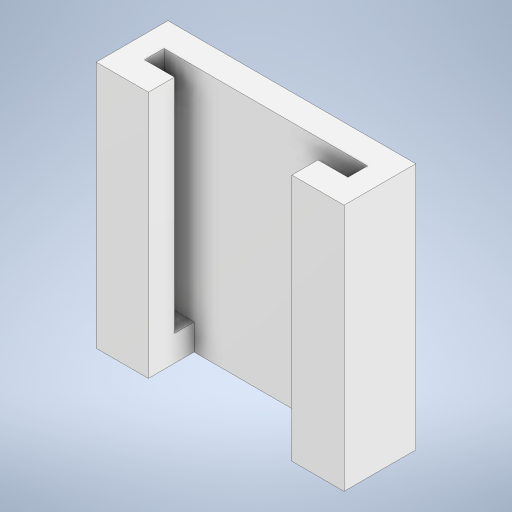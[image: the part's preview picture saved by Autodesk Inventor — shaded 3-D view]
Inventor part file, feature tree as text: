
AUTODESK INVENTOR PART (.ipt)
format: ipt  version: 2024 (Build 280153000, 153)  size: 504,320 bytes
history: native  units: mm
features: extrude x3, sketch x3, move_body x2, other x2, boolean_combine x1
ambient origin geometry x8: Origin, YZ Plane, XZ Plane, XY Plane, X Axis, Y Axis, Z Axis, Center Point
bodies: Solid1 (feature_tree), Solid2 (feature_tree)
feature tree (11):
  move_body  "Move Body1"
  move_body  "Move Body2"
  boolean_combine  "Combine1"
  extrude  "Extrusion1"  Depth=2.0mm TaperAngle=0.0deg
  extrude  "Extrusion2"  Depth=2.0mm TaperAngle=0.0deg
  extrude  "Extrusion5"  Depth=17.0mm
  sketch  "Sketch1"  dims[d0=9.5mm d1=-6.0mm d2=0.0mm d3=0.0mm d4=0.0mm d5=2.0mm]
  sketch  "Sketch2"  dims[d6=2.0mm d7=0.0mm d8=2.0mm d9=0.0mm]
  sketch  "Sketch7"  dims[d24=0.3mm d25=0.3mm d26=17.0mm d27=0.0mm d28=0.5mm d29=0.872665mm]
  other  "Part 1"
  other  "Part 1:1"
